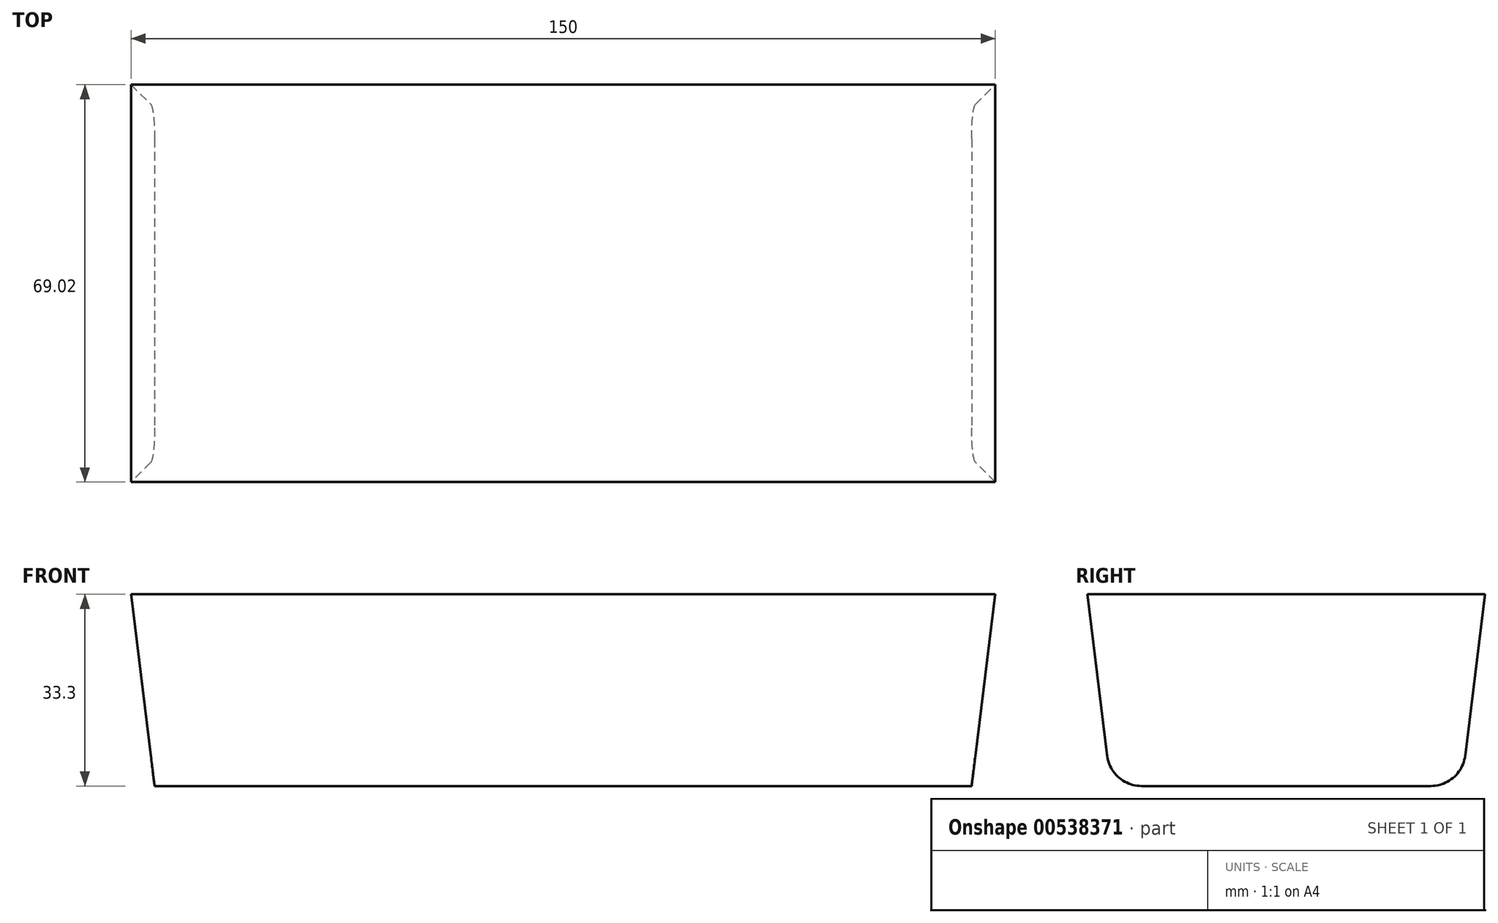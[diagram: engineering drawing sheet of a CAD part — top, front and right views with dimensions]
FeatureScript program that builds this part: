
annotation { "Feature Type Name" : "Feature", "Feature Type Description" : "" }
export const myFeature = defineFeature(function(context is Context, id is Id, definition is map)
    precondition{}
    {
        {
            var Q0;
            Q0=qCreatedBy(makeId("Right.planeOp"),FACE);
            var sketch = newSketch(context, id + "F0", { "sketchPlane" : qUnion([Q0])});
            skLineSegment(sketch, "E0", {"start": v(-40, 0) * mm, "end": v(-40, 40) * mm});
            skLineSegment(sketch, "E1", {"start": v(-40, 40) * mm, "end": v(-37, 40) * mm});
            skLineSegment(sketch, "E2", {"start": v(-34.5, 37.8) * mm, "end": v(-31.07, 9.77) * mm});
            skLineSegment(sketch, "E3", {"start": v(-25.11, 4.5) * mm, "end": v(25.11, 4.5) * mm});
            skLineSegment(sketch, "E4", {"start": v(31.07, 9.77) * mm, "end": v(34.5, 37.8) * mm});
            skLineSegment(sketch, "E5", {"start": v(37, 40) * mm, "end": v(40, 40) * mm});
            skLineSegment(sketch, "E6", {"start": v(40, 40) * mm, "end": v(40, 0) * mm});
            skLineSegment(sketch, "E7", {"start": v(40, 0) * mm, "end": v(-40, 0) * mm});
            skPoint(sketch, "E8.visualSharp", {"position": v(-34.78, 40) * mm});
            skArc(sketch, "E8.filletArc", {"start": v(-34.5, 37.8) * mm, "mid": v(-35.33, 39.37) * mm, "end": v(-37, 40) * mm});
            skPoint(sketch, "E9.visualSharp", {"position": v(-30.42, 4.5) * mm});
            skArc(sketch, "E9.filletArc", {"start": v(-31.07, 9.77) * mm, "mid": v(-29.09, 6) * mm, "end": v(-25.11, 4.5) * mm});
            skPoint(sketch, "E10.visualSharp", {"position": v(30.42, 4.5) * mm});
            skArc(sketch, "E10.filletArc", {"start": v(25.11, 4.5) * mm, "mid": v(29.09, 6) * mm, "end": v(31.07, 9.77) * mm});
            skPoint(sketch, "E11.visualSharp", {"position": v(34.78, 40) * mm});
            skArc(sketch, "E11.filletArc", {"start": v(37, 40) * mm, "mid": v(35.33, 39.37) * mm, "end": v(34.5, 37.8) * mm});
            skLineSegment(sketch, "E12", {"start": v(-40, 22.25) * mm, "end": v(-32.6, 22.25) * mm, "construction": true});
            skLineSegment(sketch, "E13", {"start": v(-34.5, 37.8) * mm, "end": v(34.5, 37.8) * mm});
            skSolve(sketch);
        }
        {
            var Q0;
            Q0=makeQuery(id+"F0.imprint","IMPRINT",FACE,{"disambiguationData":[TD([[makeQuery(id+"F0.imprint","IMPRINT",EDGE,{"derivedFrom":sQuery(id+"F0.wireOp",EDGE,"E2")}),1.0]])]});
            extrude(context, id + "F1", {"entities" : qUnion([Q0]), "depth" : 150 * mm, "offsetDistance" : 25 * mm});
        }
        {
            var Q0;
            Q0=qCreatedBy(makeId("Front.planeOp"),FACE);
            var sketch = newSketch(context, id + "F2", { "sketchPlane" : qUnion([Q0])});
            skLineSegment(sketch, "E14", {"start": v(0, 37.8) * mm, "end": v(4.09, 4.5) * mm});
            skLineSegment(sketch, "E15", {"start": v(145.91, 4.5) * mm, "end": v(150, 37.8) * mm});
            skLineSegment(sketch, "E16", {"start": v(150, 37.8) * mm, "end": v(150, 4.5) * mm});
            skLineSegment(sketch, "E17", {"start": v(0, 4.5) * mm, "end": v(0, 37.8) * mm});
            skLineSegment(sketch, "E18", {"start": v(0, 4.5) * mm, "end": v(4.09, 4.5) * mm});
            skLineSegment(sketch, "E19", {"start": v(145.91, 4.5) * mm, "end": v(150, 4.5) * mm});
            skSolve(sketch);
        }
        {
            var Q0;
            Q0 = qSketchRegion(id + "F2", true);
            extrude(context, id + "F3", {"entities" : qUnion([Q0]), "operationType" : NewBodyOperationType.REMOVE, "endBound" : BoundingType.THROUGH_ALL, "oppositeDirection" : true, "depth" : 25 * mm, "offsetDistance" : 25 * mm, "hasSecondDirection" : true, "secondDirectionBound" : SecondDirectionBoundingType.THROUGH_ALL, "secondDirectionOppositeDirection" : false, "secondDirectionDepth" : 25 * mm});
        }
    });
